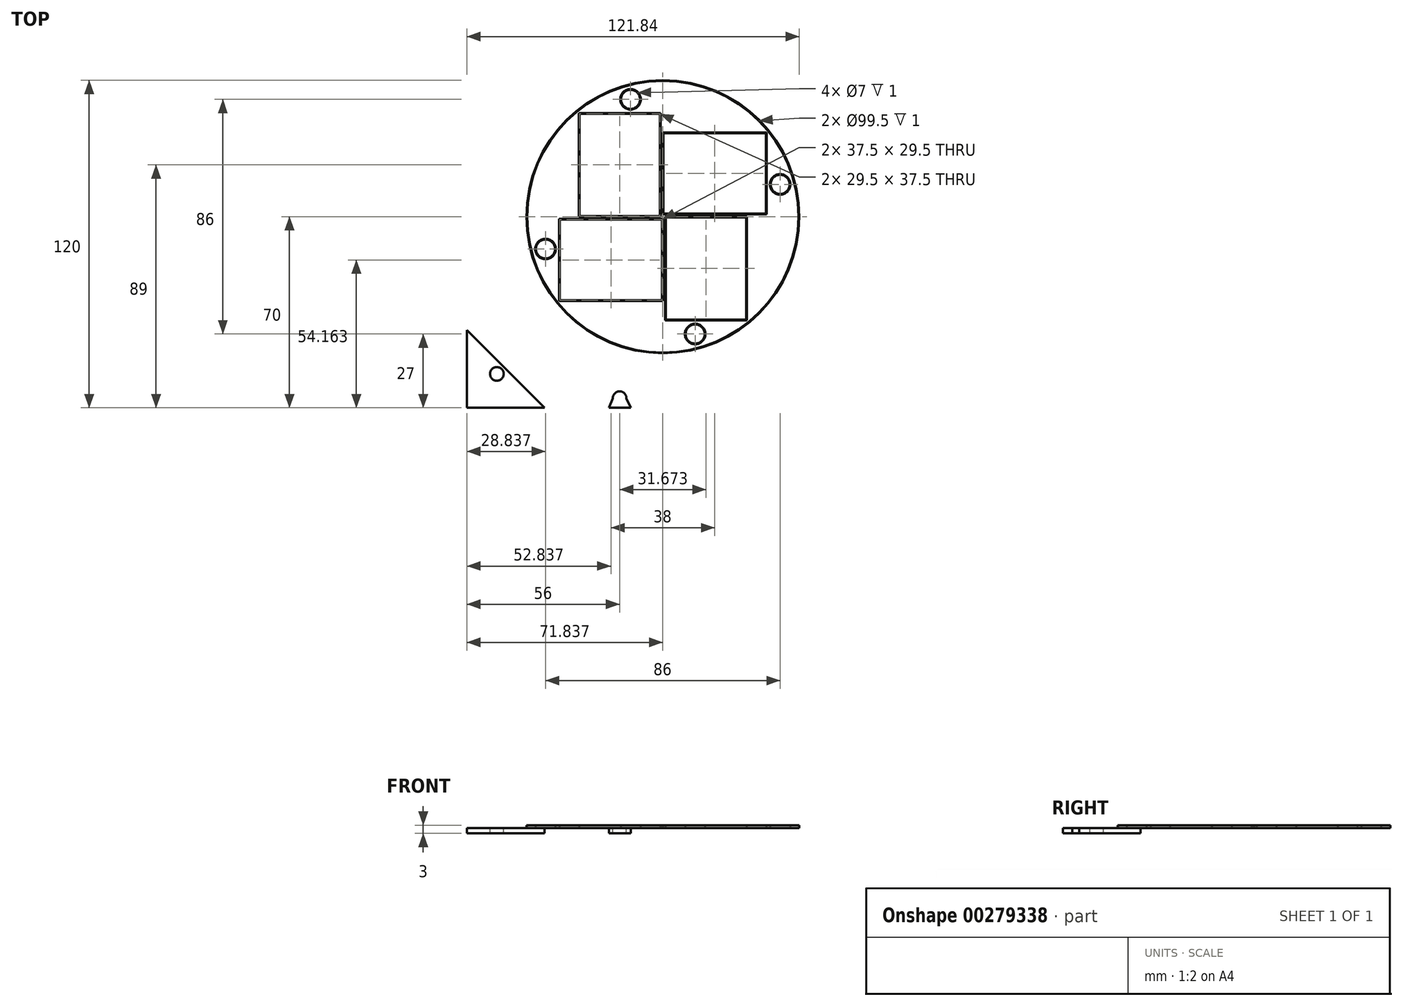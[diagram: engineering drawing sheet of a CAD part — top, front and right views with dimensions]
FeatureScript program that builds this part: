
annotation { "Feature Type Name" : "Feature", "Feature Type Description" : "" }
export const myFeature = defineFeature(function(context is Context, id is Id, definition is map)
    precondition{}
    {
        {
            var Q0;
            Q0=qCreatedBy(makeId("Top.planeOp"),FACE);
            var sketch = newSketch(context, id + "F0", { "sketchPlane" : qUnion([Q0])});
            skLineSegment(sketch, "E0.bottom", {"start": v(75, 70) * mm, "end": v(-75, 70) * mm});
            skLineSegment(sketch, "E0.top", {"start": v(75, -70) * mm, "end": v(-75, -70) * mm});
            skLineSegment(sketch, "E0.left", {"start": v(75, 70) * mm, "end": v(75, -70) * mm});
            skLineSegment(sketch, "E0.right", {"start": v(-75, 70) * mm, "end": v(-75, -70) * mm});
            skPoint(sketch, "E0.middle", {"position": v(0, 0) * mm});
            skSolve(sketch);
        }
        {
            var Q0;
            Q0=qSketchRegion(id+"F0",true);
            extrude(context, id + "F1", {"entities" : qUnion([Q0]), "depth" : 2 * mm});
        }
        {
            var Q0;
            Q0=makeQuery(id+"F1.opExtrude","CAP_FACE",FACE,{"disambiguationData":[OSD([sQuery(id+"F0.wireOp",EDGE,"E0.bottom"),sQuery(id+"F0.wireOp",EDGE,"E0.top"),sQuery(id+"F0.wireOp",EDGE,"E0.left"),sQuery(id+"F0.wireOp",EDGE,"E0.right")])],"isStart":false});
            var sketch = newSketch(context, id + "F2", { "sketchPlane" : qUnion([Q0])});
            skArc(sketch, "E1", {"start": v(-67.18, 6.35) * mm, "mid": v(-67.92, 8.12) * mm, "end": v(-69.68, 8.85) * mm});
            skArc(sketch, "E2.MirrorC", {"start": v(-67.18, -6.35) * mm, "mid": v(-67.92, -8.12) * mm, "end": v(-69.68, -8.85) * mm});
            skArc(sketch, "E3", {"start": v(-21.5, 66.52) * mm, "mid": v(-19, 64) * mm, "end": v(-16.5, 66.52) * mm});
            skCircle(sketch, "E4", {"center": v(-64, 57.6) * mm, "radius": 2.5 * mm});
            skArc(sketch, "E5.MirrorC", {"start": v(-21.5, -66.52) * mm, "mid": v(-19, -64) * mm, "end": v(-16.5, -66.52) * mm});
            skCircle(sketch, "E6.MirrorC", {"center": v(-64, -57.6) * mm, "radius": 2.5 * mm});
            skLineSegment(sketch, "E7", {"start": v(-21.5, 66.52) * mm, "end": v(-22.94, 70) * mm});
            skLineSegment(sketch, "E8.MirrorCS", {"start": v(-16.5, 66.52) * mm, "end": v(-14.88, 70) * mm});
            skLineSegment(sketch, "E9.MirrorCS", {"start": v(-16.5, -66.52) * mm, "end": v(-14.88, -70) * mm});
            skLineSegment(sketch, "E10.MirrorCS", {"start": v(-21.5, -66.52) * mm, "end": v(-22.94, -70) * mm});
            skLineSegment(sketch, "E11", {"start": v(-46.5, 70) * mm, "end": v(-75, 41.5) * mm});
            skLineSegment(sketch, "E12.MirrorCS", {"start": v(-46.5, -70) * mm, "end": v(-75, -41.5) * mm});
            skLineSegment(sketch, "E13", {"start": v(-69.68, 8.85) * mm, "end": v(-75, 8.85) * mm});
            skLineSegment(sketch, "E14", {"start": v(-67.18, -6.35) * mm, "end": v(-67.18, 6.35) * mm});
            skLineSegment(sketch, "E15.MirrorCS", {"start": v(-69.68, -8.85) * mm, "end": v(-75, -8.85) * mm});
            skSolve(sketch);
        }
        {
            var Q0;
            Q0=qSketchRegion(id+"F2",true);
            var Q1;
            Q1=makeQuery(id+"F2.imprint","IMPRINT",FACE,{"disambiguationData":[TD([[makeQuery(id+"F2.imprint","IMPRINT",EDGE,{"derivedFrom":sQuery(id+"F2.wireOp",EDGE,"E4")}),-1.0]])]});
            var Q2;
            Q2=makeQuery(id+"F2.imprint","IMPRINT",FACE,{"disambiguationData":[TD([[makeQuery(id+"F2.imprint","IMPRINT",EDGE,{"derivedFrom":sQuery(id+"F2.wireOp",EDGE,"E1")}),1.0]])]});
            var Q3;
            Q3=makeQuery(id+"F2.imprint","IMPRINT",FACE,{"disambiguationData":[TD([[makeQuery(id+"F2.imprint","IMPRINT",EDGE,{"derivedFrom":sQuery(id+"F2.wireOp",EDGE,"E5.MirrorC")}),-1.0]])]});
            var Q4;
            Q4=makeQuery(id+"F2.imprint","IMPRINT",FACE,{"disambiguationData":[TD([[makeQuery(id+"F2.imprint","IMPRINT",EDGE,{"derivedFrom":sQuery(id+"F2.wireOp",EDGE,"E3")}),1.0]])]});
            var Q5;
            Q5=makeQuery(id+"F2.imprint","IMPRINT",FACE,{"disambiguationData":[TD([[makeQuery(id+"F2.imprint","IMPRINT",EDGE,{"derivedFrom":sQuery(id+"F2.wireOp",EDGE,"E6.MirrorC")}),1.0]])]});
            extrude(context, id + "F3", {"entities" : qUnion([Q0, Q1, Q2, Q3, Q4, Q5]), "operationType" : NewBodyOperationType.REMOVE, "oppositeDirection" : true, "depth" : 5 * mm});
        }
        {
            var Q0;
            Q0=makeQuery(id+"F1.opExtrude","CAP_FACE",FACE,{"disambiguationData":[OSD([sQuery(id+"F0.wireOp",EDGE,"E0.bottom"),sQuery(id+"F0.wireOp",EDGE,"E0.top"),sQuery(id+"F0.wireOp",EDGE,"E0.left"),sQuery(id+"F0.wireOp",EDGE,"E0.right")])],"isStart":false});
            var sketch = newSketch(context, id + "F4", { "sketchPlane" : qUnion([Q0])});
            skCircle(sketch, "E16", {"center": v(-3.16, 0) * mm, "radius": 50 * mm});
            skCircle(sketch, "E17", {"center": v(-3.16, 0) * mm, "radius": 49.5 * mm});
            skCircle(sketch, "E18", {"center": v(-3.16, 0) * mm, "radius": 49.75 * mm});
            skLineSegment(sketch, "E19.bottom", {"start": v(-4, 38) * mm, "end": v(-34, 38) * mm});
            skLineSegment(sketch, "E19.top", {"start": v(-4, 0) * mm, "end": v(-34, 0) * mm});
            skLineSegment(sketch, "E19.left", {"start": v(-4, 38) * mm, "end": v(-4, 0) * mm});
            skLineSegment(sketch, "E19.right", {"start": v(-34, 38) * mm, "end": v(-34, 0) * mm});
            skPoint(sketch, "E19.middle", {"position": v(-19, 19) * mm});
            skLineSegment(sketch, "E20.bottom", {"start": v(-4.25, 37.75) * mm, "end": v(-33.75, 37.75) * mm});
            skLineSegment(sketch, "E20.top", {"start": v(-4.25, 0.25) * mm, "end": v(-33.75, 0.25) * mm});
            skLineSegment(sketch, "E20.left", {"start": v(-4.25, 37.75) * mm, "end": v(-4.25, 0.25) * mm});
            skLineSegment(sketch, "E20.right", {"start": v(-33.75, 37.75) * mm, "end": v(-33.75, 0.25) * mm});
            skCircle(sketch, "E21", {"center": v(-15, 43) * mm, "radius": 3.75 * mm});
            skCircle(sketch, "E22", {"center": v(-15, 43) * mm, "radius": 3.5 * mm});
            skLineSegment(sketch, "E23.1.0", {"start": v(-41.16, -0.84) * mm, "end": v(-3.16, -0.84) * mm});
            skLineSegment(sketch, "E23.1.1", {"start": v(-40.91, -1.09) * mm, "end": v(-3.41, -1.09) * mm});
            skLineSegment(sketch, "E23.1.2", {"start": v(-40.91, -1.09) * mm, "end": v(-40.91, -30.59) * mm});
            skLineSegment(sketch, "E23.1.3", {"start": v(-41.16, -0.84) * mm, "end": v(-41.16, -30.84) * mm});
            skLineSegment(sketch, "E23.1.4", {"start": v(-40.91, -30.59) * mm, "end": v(-3.41, -30.59) * mm});
            skLineSegment(sketch, "E23.1.5", {"start": v(-41.16, -30.84) * mm, "end": v(-3.16, -30.84) * mm});
            skLineSegment(sketch, "E23.1.6", {"start": v(-3.16, -0.84) * mm, "end": v(-3.16, -30.84) * mm});
            skLineSegment(sketch, "E23.1.7", {"start": v(-3.41, -1.09) * mm, "end": v(-3.41, -30.59) * mm});
            skCircle(sketch, "E23.1.8", {"center": v(-46.16, -11.84) * mm, "radius": 3.5 * mm});
            skCircle(sketch, "E23.1.9", {"center": v(-46.16, -11.84) * mm, "radius": 3.75 * mm});
            skLineSegment(sketch, "E23.2.0", {"start": v(-2.33, -38) * mm, "end": v(-2.33, 0) * mm});
            skLineSegment(sketch, "E23.2.1", {"start": v(-2.08, -37.75) * mm, "end": v(-2.08, -0.25) * mm});
            skLineSegment(sketch, "E23.2.2", {"start": v(-2.08, -37.75) * mm, "end": v(27.42, -37.75) * mm});
            skLineSegment(sketch, "E23.2.3", {"start": v(-2.33, -38) * mm, "end": v(27.67, -38) * mm});
            skLineSegment(sketch, "E23.2.4", {"start": v(27.42, -37.75) * mm, "end": v(27.42, -0.25) * mm});
            skLineSegment(sketch, "E23.2.5", {"start": v(27.67, -38) * mm, "end": v(27.67, 0) * mm});
            skLineSegment(sketch, "E23.2.6", {"start": v(-2.33, 0) * mm, "end": v(27.67, 0) * mm});
            skLineSegment(sketch, "E23.2.7", {"start": v(-2.08, -0.25) * mm, "end": v(27.42, -0.25) * mm});
            skCircle(sketch, "E23.2.8", {"center": v(8.67, -43) * mm, "radius": 3.5 * mm});
            skCircle(sketch, "E23.2.9", {"center": v(8.67, -43) * mm, "radius": 3.75 * mm});
            skLineSegment(sketch, "E23.3.0", {"start": v(34.84, 0.84) * mm, "end": v(-3.16, 0.84) * mm});
            skLineSegment(sketch, "E23.3.1", {"start": v(34.59, 1.09) * mm, "end": v(-2.91, 1.09) * mm});
            skLineSegment(sketch, "E23.3.2", {"start": v(34.59, 1.09) * mm, "end": v(34.59, 30.59) * mm});
            skLineSegment(sketch, "E23.3.3", {"start": v(34.84, 0.84) * mm, "end": v(34.84, 30.84) * mm});
            skLineSegment(sketch, "E23.3.4", {"start": v(34.59, 30.59) * mm, "end": v(-2.91, 30.59) * mm});
            skLineSegment(sketch, "E23.3.5", {"start": v(34.84, 30.84) * mm, "end": v(-3.16, 30.84) * mm});
            skLineSegment(sketch, "E23.3.6", {"start": v(-3.16, 0.84) * mm, "end": v(-3.16, 30.84) * mm});
            skLineSegment(sketch, "E23.3.7", {"start": v(-2.91, 1.09) * mm, "end": v(-2.91, 30.59) * mm});
            skCircle(sketch, "E23.3.8", {"center": v(39.84, 11.84) * mm, "radius": 3.5 * mm});
            skCircle(sketch, "E23.3.9", {"center": v(39.84, 11.84) * mm, "radius": 3.75 * mm});
            skSolve(sketch);
        }
        {
            var Q0;
            Q0=qSketchRegion(id+"F4",true);
            var Q1;
            Q1=makeQuery(id+"F4.imprint","IMPRINT",FACE,{"disambiguationData":[TD([[makeQuery(id+"F4.imprint","IMPRINT",EDGE,{"derivedFrom":sQuery(id+"F4.wireOp",EDGE,"pkoXZPiR-0mkQ-UggU-QeDQ-18WsZVd6IxUX")}),1.0]])]});
            var Q2;
            Q2=makeQuery(id+"F4.imprint","IMPRINT",FACE,{"disambiguationData":[TD([[makeQuery(id+"F4.imprint","IMPRINT",EDGE,{"derivedFrom":sQuery(id+"F4.wireOp",EDGE,"K1UoebT6-E9hS-h827-5MM4-wNKjuZ17nWzt.bottom")}),-1.0]])]});
            var Q3;
            Q3=makeQuery(id+"F4.imprint","IMPRINT",FACE,{"disambiguationData":[TD([[makeQuery(id+"F4.imprint","IMPRINT",EDGE,{"derivedFrom":sQuery(id+"F4.wireOp",EDGE,"6895091a-fd66-4955-bf57-3f23905b837a.3.0")}),1.0]])]});
            var Q4;
            Q4=makeQuery(id+"F4.imprint","IMPRINT",FACE,{"disambiguationData":[TD([[makeQuery(id+"F4.imprint","IMPRINT",EDGE,{"derivedFrom":sQuery(id+"F4.wireOp",EDGE,"2bf1c8c4-409d-43ad-88c8-fcb9e33b7025.3.0")}),1.0]])]});
            var Q5;
            Q5=makeQuery(id+"F4.imprint","IMPRINT",FACE,{"disambiguationData":[TD([[makeQuery(id+"F4.imprint","IMPRINT",EDGE,{"derivedFrom":sQuery(id+"F4.wireOp",EDGE,"6895091a-fd66-4955-bf57-3f23905b837a.2.0")}),1.0]])]});
            var Q6;
            Q6=makeQuery(id+"F4.imprint","IMPRINT",FACE,{"disambiguationData":[TD([[makeQuery(id+"F4.imprint","IMPRINT",EDGE,{"derivedFrom":sQuery(id+"F4.wireOp",EDGE,"2bf1c8c4-409d-43ad-88c8-fcb9e33b7025.2.0")}),1.0]])]});
            var Q7;
            Q7=makeQuery(id+"F4.imprint","IMPRINT",FACE,{"disambiguationData":[TD([[makeQuery(id+"F4.imprint","IMPRINT",EDGE,{"derivedFrom":sQuery(id+"F4.wireOp",EDGE,"6895091a-fd66-4955-bf57-3f23905b837a.1.0")}),1.0]])]});
            var Q8;
            Q8=makeQuery(id+"F4.imprint","IMPRINT",FACE,{"disambiguationData":[TD([[makeQuery(id+"F4.imprint","IMPRINT",EDGE,{"derivedFrom":sQuery(id+"F4.wireOp",EDGE,"2bf1c8c4-409d-43ad-88c8-fcb9e33b7025.1.0")}),1.0]])]});
            extrude(context, id + "F5", {"entities" : qUnion([Q0, Q1, Q2, Q3, Q4, Q5, Q6, Q7, Q8]), "depth" : 1 * mm});
        }
        {
            var Q0;
            Q0 = qSketchRegion(id + "F4", true);
            var Q1;
            Q1=makeQuery(id+"F4.imprint","IMPRINT",FACE,{"disambiguationData":[TD([[makeQuery(id+"F4.imprint","IMPRINT",EDGE,{"derivedFrom":sQuery(id+"F4.wireOp",EDGE,"E23.1.0")}),-1.0]])]});
            var Q2;
            Q2=makeQuery(id+"F4.imprint","IMPRINT",FACE,{"disambiguationData":[TD([[makeQuery(id+"F4.imprint","IMPRINT",EDGE,{"derivedFrom":sQuery(id+"F4.wireOp",EDGE,"E23.1.8")}),-1.0]])]});
            var Q3;
            Q3=makeQuery(id+"F4.imprint","IMPRINT",FACE,{"disambiguationData":[TD([[makeQuery(id+"F4.imprint","IMPRINT",EDGE,{"derivedFrom":sQuery(id+"F4.wireOp",EDGE,"E19.bottom")}),1.0]])]});
            var Q4;
            Q4=makeQuery(id+"F4.imprint","IMPRINT",FACE,{"disambiguationData":[TD([[makeQuery(id+"F4.imprint","IMPRINT",EDGE,{"derivedFrom":sQuery(id+"F4.wireOp",EDGE,"E23.3.0")}),-1.0]])]});
            var Q5;
            Q5=makeQuery(id+"F4.imprint","IMPRINT",FACE,{"disambiguationData":[TD([[makeQuery(id+"F4.imprint","IMPRINT",EDGE,{"derivedFrom":sQuery(id+"F4.wireOp",EDGE,"E23.2.0")}),-1.0]])]});
            var Q6;
            Q6=makeQuery(id+"F4.imprint","IMPRINT",FACE,{"disambiguationData":[TD([[makeQuery(id+"F4.imprint","IMPRINT",EDGE,{"derivedFrom":sQuery(id+"F4.wireOp",EDGE,"E23.3.8")}),-1.0]])]});
            var Q7;
            Q7=makeQuery(id+"F4.imprint","IMPRINT",FACE,{"disambiguationData":[TD([[makeQuery(id+"F4.imprint","IMPRINT",EDGE,{"derivedFrom":sQuery(id+"F4.wireOp",EDGE,"E23.2.8")}),-1.0]])]});
            var Q8;
            Q8=makeQuery(id+"F4.imprint","IMPRINT",FACE,{"disambiguationData":[TD([[makeQuery(id+"F4.imprint","IMPRINT",EDGE,{"derivedFrom":sQuery(id+"F4.wireOp",EDGE,"E21")}),1.0]])]});
            extrude(context, id + "F6", {"entities" : qUnion([Q0, Q1, Q2, Q3, Q4, Q5, Q6, Q7, Q8]), "depth" : 1 * mm});
        }
    });
